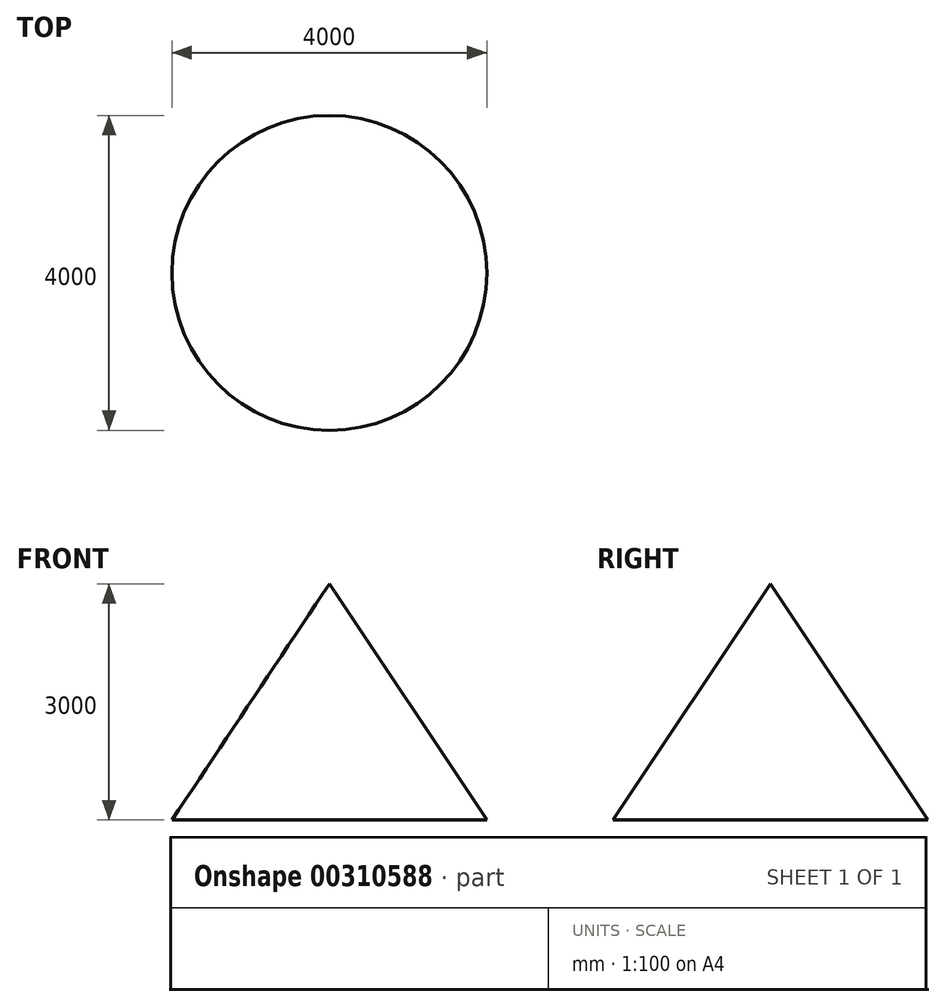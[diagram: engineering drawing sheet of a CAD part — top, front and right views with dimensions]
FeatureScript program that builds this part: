
annotation { "Feature Type Name" : "Feature", "Feature Type Description" : "" }
export const myFeature = defineFeature(function(context is Context, id is Id, definition is map)
    precondition{}
    {
        {
            var Q0;
            Q0=qCreatedBy(makeId("Front.planeOp"),FACE);
            var sketch = newSketch(context, id + "F0", { "sketchPlane" : qUnion([Q0])});
            skLineSegment(sketch, "E0", {"start": v(0, 0) * mm, "end": v(-2000, 0) * mm});
            skLineSegment(sketch, "E1", {"start": v(0, 0) * mm, "end": v(0, 3000) * mm});
            skLineSegment(sketch, "E2", {"start": v(-2000, 0) * mm, "end": v(0, 3000) * mm});
            skLineSegment(sketch, "E3", {"start": v(0, -2907.7) * mm, "end": v(0, 4400.66) * mm, "construction": true});
            skSolve(sketch);
        }
        {
            var Q0;
            Q0=makeQuery(id+"F0.imprint","IMPRINT",FACE,{"disambiguationData":[TD([[makeQuery(id+"F0.imprint","IMPRINT",EDGE,{"derivedFrom":sQuery(id+"F0.wireOp",EDGE,"E0")}),-1.0]])]});
            var Q1;
            Q1=sQuery(id+"F0.wireOp",EDGE,"E3");
            revolve(context, id + "F1", {"entities" : qUnion([Q0]), "axis" : qUnion([Q1]), "revolveType" : RevolveType.FULL});
        }
    });
